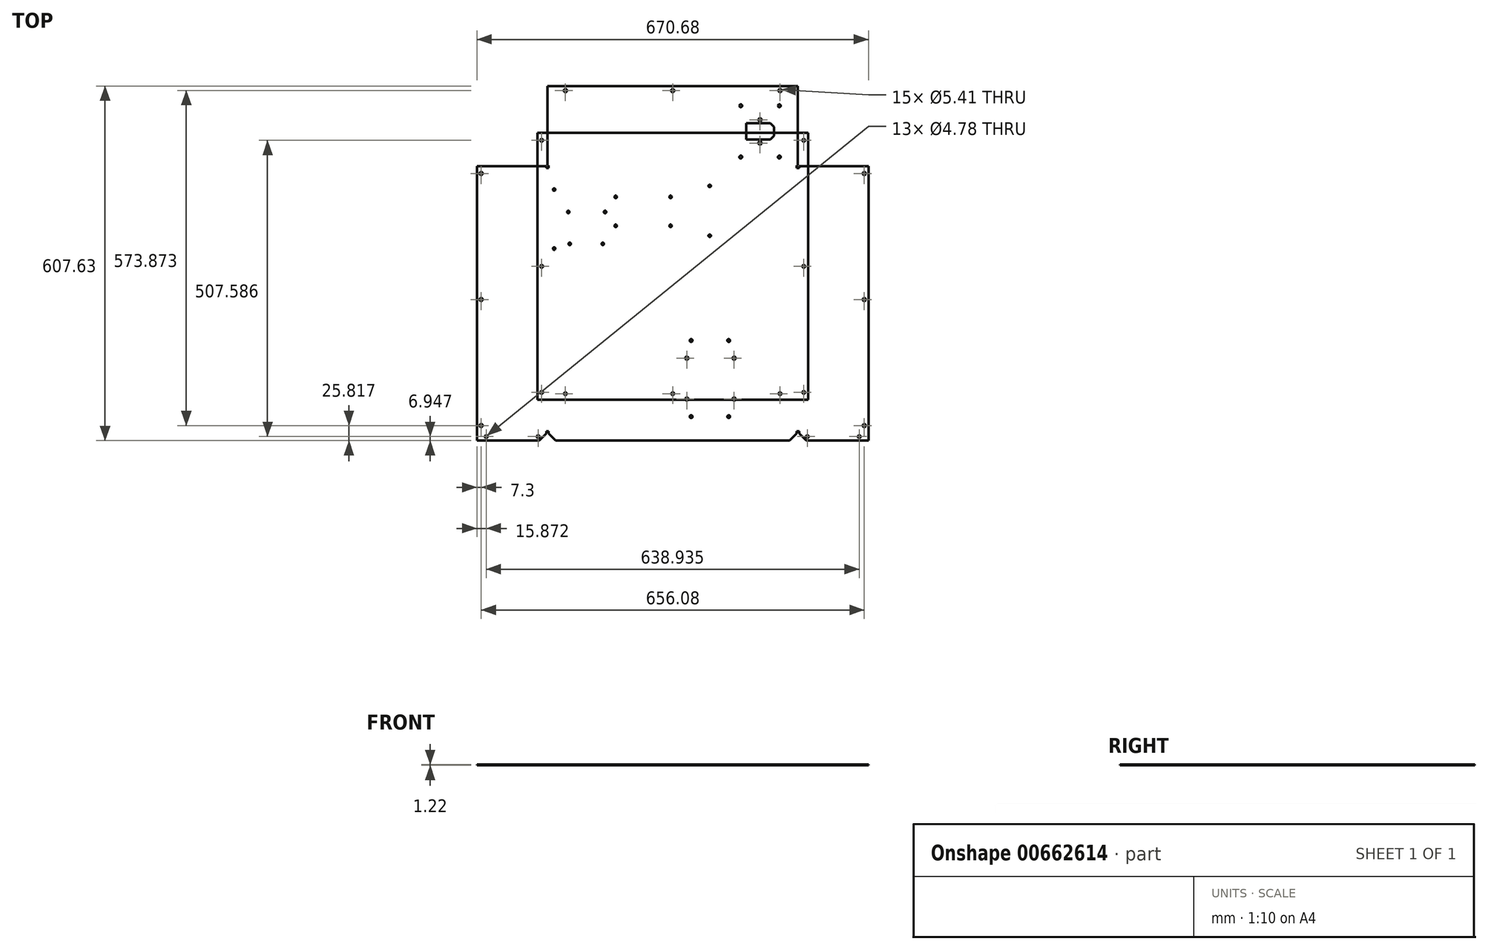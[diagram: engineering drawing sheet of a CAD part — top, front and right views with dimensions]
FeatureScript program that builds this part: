
annotation { "Feature Type Name" : "Feature", "Feature Type Description" : "" }
export const myFeature = defineFeature(function(context is Context, id is Id, definition is map)
    precondition{}
    {
        {
            var Q0;
            Q0=qCreatedBy(makeId("Top.planeOp"),FACE);
            var sketch = newSketch(context, id + "F0", { "sketchPlane" : qUnion([Q0])});
            skLineSegment(sketch, "E0", {"start": v(214.48, -268.44) * mm, "end": v(214.48, 182.35) * mm});
            skLineSegment(sketch, "E1", {"start": v(212.34, 184.5) * mm, "end": v(-212.34, 184.5) * mm});
            skLineSegment(sketch, "E2", {"start": v(335.34, 185.56) * mm, "end": v(216.63, 185.56) * mm});
            skLineSegment(sketch, "E3", {"start": v(335.34, 185.56) * mm, "end": v(335.34, -269.15) * mm});
            skLineSegment(sketch, "E4", {"start": v(335.34, -269.15) * mm, "end": v(216.65, -269.15) * mm});
            skLineSegment(sketch, "E5", {"start": v(216.65, -269.15) * mm, "end": v(216.65, -268.44) * mm});
            skLineSegment(sketch, "E6", {"start": v(216.65, -268.44) * mm, "end": v(215.91, -268.44) * mm});
            skLineSegment(sketch, "E7", {"start": v(215.91, 182.35) * mm, "end": v(215.91, -268.44) * mm});
            skLineSegment(sketch, "E8", {"start": v(215.91, 182.35) * mm, "end": v(216.63, 182.35) * mm});
            skLineSegment(sketch, "E9", {"start": v(216.63, 182.35) * mm, "end": v(216.63, 185.56) * mm});
            skCircle(sketch, "E10", {"center": v(328.04, 172.86) * mm, "radius": 2.7 * mm});
            skCircle(sketch, "E11", {"center": v(328.04, -43.04) * mm, "radius": 2.7 * mm});
            skCircle(sketch, "E12", {"center": v(328.04, -258.94) * mm, "radius": 2.7 * mm});
            skLineSegment(sketch, "E13", {"start": v(-335.34, -269.15) * mm, "end": v(-216.65, -269.15) * mm});
            skLineSegment(sketch, "E14", {"start": v(-335.34, -269.15) * mm, "end": v(-335.34, 185.56) * mm});
            skLineSegment(sketch, "E15", {"start": v(-335.34, 185.56) * mm, "end": v(-216.63, 185.56) * mm});
            skLineSegment(sketch, "E16", {"start": v(-216.63, 185.56) * mm, "end": v(-216.63, 182.35) * mm});
            skLineSegment(sketch, "E17", {"start": v(-215.91, -268.44) * mm, "end": v(-215.91, 182.35) * mm});
            skLineSegment(sketch, "E18", {"start": v(-215.91, -268.44) * mm, "end": v(-216.65, -268.44) * mm});
            skLineSegment(sketch, "E19", {"start": v(-216.65, -268.44) * mm, "end": v(-216.65, -269.15) * mm});
            skCircle(sketch, "E20", {"center": v(-328.04, 172.86) * mm, "radius": 2.7 * mm});
            skCircle(sketch, "E21", {"center": v(-328.04, -43.04) * mm, "radius": 2.7 * mm});
            skCircle(sketch, "E22", {"center": v(-328.04, -258.94) * mm, "radius": 2.7 * mm});
            skLineSegment(sketch, "E23", {"start": v(-216.63, 182.35) * mm, "end": v(-215.91, 182.35) * mm});
            skLineSegment(sketch, "E24", {"start": v(-228.68, -284.76) * mm, "end": v(-216.64, -272.72) * mm});
            skLineSegment(sketch, "E25", {"start": v(-335.34, -284.76) * mm, "end": v(-228.68, -284.76) * mm});
            skLineSegment(sketch, "E26", {"start": v(-335.34, -272.01) * mm, "end": v(-335.34, -284.76) * mm});
            skLineSegment(sketch, "E27", {"start": v(-335.34, -272.01) * mm, "end": v(-216.65, -272.01) * mm});
            skLineSegment(sketch, "E28", {"start": v(-216.65, -272.01) * mm, "end": v(-216.65, -272.72) * mm});
            skLineSegment(sketch, "E29", {"start": v(-216.65, -272.72) * mm, "end": v(-216.64, -272.72) * mm});
            skCircle(sketch, "E30", {"center": v(-230.57, -277.81) * mm, "radius": 2.39 * mm});
            skCircle(sketch, "E31", {"center": v(-319.47, -277.81) * mm, "radius": 2.39 * mm});
            skLineSegment(sketch, "E32", {"start": v(216.65, -272.01) * mm, "end": v(216.65, -269.15) * mm});
            skLineSegment(sketch, "E33", {"start": v(335.34, -269.15) * mm, "end": v(335.34, -272.01) * mm});
            skLineSegment(sketch, "E34", {"start": v(335.34, -272.01) * mm, "end": v(216.65, -272.01) * mm});
            skLineSegment(sketch, "E35", {"start": v(-216.65, -269.15) * mm, "end": v(-216.65, -272.01) * mm});
            skLineSegment(sketch, "E36", {"start": v(-335.34, -272.01) * mm, "end": v(-335.34, -269.15) * mm});
            skLineSegment(sketch, "E37", {"start": v(-214.3, 304.14) * mm, "end": v(214.3, 304.14) * mm});
            skLineSegment(sketch, "E38", {"start": v(214.3, 304.14) * mm, "end": v(214.3, 186.64) * mm});
            skLineSegment(sketch, "E39", {"start": v(214.3, 186.64) * mm, "end": v(212.34, 186.64) * mm});
            skLineSegment(sketch, "E40", {"start": v(212.34, 186.64) * mm, "end": v(212.34, 185.92) * mm});
            skLineSegment(sketch, "E41", {"start": v(-212.34, 185.92) * mm, "end": v(212.34, 185.92) * mm});
            skLineSegment(sketch, "E42", {"start": v(-212.34, 185.92) * mm, "end": v(-212.34, 186.64) * mm});
            skLineSegment(sketch, "E43", {"start": v(-212.34, 186.64) * mm, "end": v(-214.3, 186.64) * mm});
            skLineSegment(sketch, "E44", {"start": v(125.77, 231.19) * mm, "end": v(166.92, 231.19) * mm});
            skLineSegment(sketch, "E45", {"start": v(166.92, 231.19) * mm, "end": v(173.27, 237.54) * mm});
            skLineSegment(sketch, "E46", {"start": v(173.27, 237.54) * mm, "end": v(173.27, 252.52) * mm});
            skLineSegment(sketch, "E47", {"start": v(173.27, 252.52) * mm, "end": v(166.92, 258.87) * mm});
            skLineSegment(sketch, "E48", {"start": v(166.92, 258.87) * mm, "end": v(125.77, 258.87) * mm});
            skLineSegment(sketch, "E49", {"start": v(125.77, 258.87) * mm, "end": v(125.77, 231.19) * mm});
            skCircle(sketch, "E50", {"center": v(149.52, 264.97) * mm, "radius": 2.7 * mm});
            skCircle(sketch, "E51", {"center": v(149.52, 225.1) * mm, "radius": 2.7 * mm});
            skCircle(sketch, "E52", {"center": v(182.55, 288.93) * mm, "radius": 2.4 * mm});
            skCircle(sketch, "E53", {"center": v(182.55, 201.13) * mm, "radius": 2.4 * mm});
            skCircle(sketch, "E54", {"center": v(116.48, 288.93) * mm, "radius": 2.4 * mm});
            skCircle(sketch, "E55", {"center": v(116.48, 201.13) * mm, "radius": 2.4 * mm});
            skLineSegment(sketch, "E56", {"start": v(-214.3, 304.14) * mm, "end": v(-214.3, 186.64) * mm});
            skLineSegment(sketch, "E57", {"start": v(-213.06, -268.44) * mm, "end": v(-215.91, -268.44) * mm});
            skLineSegment(sketch, "E58", {"start": v(-213.06, -268.44) * mm, "end": v(-213.06, 182.35) * mm});
            skLineSegment(sketch, "E59", {"start": v(-215.91, 182.35) * mm, "end": v(-213.06, 182.35) * mm});
            skLineSegment(sketch, "E60", {"start": v(-214.3, 307) * mm, "end": v(214.3, 307) * mm});
            skLineSegment(sketch, "E61", {"start": v(214.3, 307) * mm, "end": v(214.3, 304.14) * mm});
            skLineSegment(sketch, "E62", {"start": v(-214.3, 304.14) * mm, "end": v(-214.3, 307) * mm});
            skCircle(sketch, "E63", {"center": v(-183.8, 314.93) * mm, "radius": 2.7 * mm});
            skCircle(sketch, "E64", {"center": v(0, 314.93) * mm, "radius": 2.7 * mm});
            skLineSegment(sketch, "E65", {"start": v(214.3, 322.87) * mm, "end": v(-214.3, 322.87) * mm});
            skLineSegment(sketch, "E66", {"start": v(214.3, 307) * mm, "end": v(214.3, 322.87) * mm});
            skLineSegment(sketch, "E67", {"start": v(-214.3, 322.87) * mm, "end": v(-214.3, 307) * mm});
            skCircle(sketch, "E68", {"center": v(183.8, 314.93) * mm, "radius": 2.7 * mm});
            skLineSegment(sketch, "E69", {"start": v(-212.34, 183.07) * mm, "end": v(-212.34, 185.92) * mm});
            skLineSegment(sketch, "E70", {"start": v(212.34, 185.92) * mm, "end": v(212.34, 183.07) * mm});
            skLineSegment(sketch, "E71", {"start": v(-212.34, 183.07) * mm, "end": v(212.34, 183.07) * mm});
            skLineSegment(sketch, "E72", {"start": v(212.31, -269.15) * mm, "end": v(212.31, -272.01) * mm});
            skLineSegment(sketch, "E73", {"start": v(212.31, -272.01) * mm, "end": v(-212.31, -272.01) * mm});
            skLineSegment(sketch, "E74", {"start": v(-212.31, -272.01) * mm, "end": v(-212.31, -269.15) * mm});
            skLineSegment(sketch, "E75", {"start": v(212.31, -269.15) * mm, "end": v(-212.31, -269.15) * mm});
            skLineSegment(sketch, "E76", {"start": v(212.34, 182.35) * mm, "end": v(212.34, 183.07) * mm});
            skLineSegment(sketch, "E77", {"start": v(213.06, 182.35) * mm, "end": v(212.34, 182.35) * mm});
            skLineSegment(sketch, "E78", {"start": v(213.06, 182.35) * mm, "end": v(213.06, -268.44) * mm});
            skLineSegment(sketch, "E79", {"start": v(212.31, -268.44) * mm, "end": v(213.06, -268.44) * mm});
            skLineSegment(sketch, "E80", {"start": v(-212.31, -268.44) * mm, "end": v(-212.31, -269.15) * mm});
            skLineSegment(sketch, "E81", {"start": v(-212.34, 182.35) * mm, "end": v(-213.06, 182.35) * mm});
            skLineSegment(sketch, "E82", {"start": v(-212.34, 183.07) * mm, "end": v(-212.34, 182.35) * mm});
            skCircle(sketch, "E83", {"center": v(-203.02, 145.28) * mm, "radius": 2.1 * mm});
            skCircle(sketch, "E84", {"center": v(-203.02, 44.24) * mm, "radius": 2.1 * mm});
            skCircle(sketch, "E85", {"center": v(-176.36, 52.4) * mm, "radius": 2.1 * mm});
            skCircle(sketch, "E86", {"center": v(-119.8, 52.4) * mm, "radius": 2.1 * mm});
            skCircle(sketch, "E87", {"center": v(-97.68, 83.35) * mm, "radius": 2.1 * mm});
            skCircle(sketch, "E88", {"center": v(-178.86, 107) * mm, "radius": 2.1 * mm});
            skCircle(sketch, "E89", {"center": v(-115.92, 107) * mm, "radius": 2.1 * mm});
            skCircle(sketch, "E90", {"center": v(-97.68, 132.88) * mm, "radius": 2.1 * mm});
            skCircle(sketch, "E91", {"center": v(-3.7, 132.88) * mm, "radius": 2.1 * mm});
            skCircle(sketch, "E92", {"center": v(63.33, 66.23) * mm, "radius": 2.1 * mm});
            skCircle(sketch, "E93", {"center": v(63.32, 151.64) * mm, "radius": 2.1 * mm});
            skCircle(sketch, "E94", {"center": v(-3.7, 83.35) * mm, "radius": 2.1 * mm});
            skCircle(sketch, "E95", {"center": v(24.15, -143.4) * mm, "radius": 2.7 * mm});
            skCircle(sketch, "E96", {"center": v(24.15, -213.4) * mm, "radius": 2.7 * mm});
            skCircle(sketch, "E97", {"center": v(105.15, -213.4) * mm, "radius": 2.7 * mm});
            skCircle(sketch, "E98", {"center": v(105.15, -143.4) * mm, "radius": 2.7 * mm});
            skCircle(sketch, "E99", {"center": v(31.5, -243.62) * mm, "radius": 2.4 * mm});
            skCircle(sketch, "E100", {"center": v(95.85, -243.62) * mm, "radius": 2.4 * mm});
            skCircle(sketch, "E101", {"center": v(31.5, -113.2) * mm, "radius": 2.4 * mm});
            skCircle(sketch, "E102", {"center": v(95.85, -113.2) * mm, "radius": 2.4 * mm});
            skLineSegment(sketch, "E103", {"start": v(212.31, -269.15) * mm, "end": v(212.31, -268.44) * mm});
            skLineSegment(sketch, "E104", {"start": v(-213.06, -268.44) * mm, "end": v(-212.31, -268.44) * mm});
            skLineSegment(sketch, "E105", {"start": v(215.91, -268.44) * mm, "end": v(213.06, -268.44) * mm});
            skLineSegment(sketch, "E106", {"start": v(213.06, 182.35) * mm, "end": v(215.91, 182.35) * mm});
            skLineSegment(sketch, "E107", {"start": v(335.34, -284.76) * mm, "end": v(335.34, -272.01) * mm});
            skLineSegment(sketch, "E108", {"start": v(228.68, -284.76) * mm, "end": v(335.34, -284.76) * mm});
            skLineSegment(sketch, "E109", {"start": v(216.65, -272.72) * mm, "end": v(216.65, -272.01) * mm});
            skCircle(sketch, "E110", {"center": v(230.57, -277.81) * mm, "radius": 2.39 * mm});
            skCircle(sketch, "E111", {"center": v(319.47, -277.81) * mm, "radius": 2.39 * mm});
            skLineSegment(sketch, "E112", {"start": v(216.64, -272.72) * mm, "end": v(228.68, -284.76) * mm});
            skLineSegment(sketch, "E113", {"start": v(216.64, -272.72) * mm, "end": v(216.65, -272.72) * mm});
            skLineSegment(sketch, "E114", {"start": v(212.31, -272.01) * mm, "end": v(212.31, -272.72) * mm});
            skLineSegment(sketch, "E115", {"start": v(-212.31, -272.72) * mm, "end": v(-212.31, -272.01) * mm});
            skLineSegment(sketch, "E116", {"start": v(-200.29, -284.76) * mm, "end": v(200.29, -284.76) * mm});
            skLineSegment(sketch, "E117", {"start": v(-200.29, -284.76) * mm, "end": v(-212.32, -272.72) * mm});
            skLineSegment(sketch, "E118", {"start": v(-212.32, -272.72) * mm, "end": v(-212.31, -272.72) * mm});
            skLineSegment(sketch, "E119", {"start": v(212.31, -272.72) * mm, "end": v(212.32, -272.72) * mm});
            skLineSegment(sketch, "E120", {"start": v(212.32, -272.72) * mm, "end": v(200.29, -284.76) * mm});
            skLineSegment(sketch, "E121", {"start": v(212.31, -270.58) * mm, "end": v(-212.31, -270.58) * mm});
            skLineSegment(sketch, "E122", {"start": v(-214.48, -268.44) * mm, "end": v(-214.48, 182.35) * mm});
            skLineSegment(sketch, "E123", {"start": v(-214.3, 305.56) * mm, "end": v(214.3, 305.56) * mm});
            skLineSegment(sketch, "E124", {"start": v(335.34, -270.58) * mm, "end": v(216.65, -270.58) * mm});
            skLineSegment(sketch, "E125", {"start": v(-335.34, -270.58) * mm, "end": v(-216.65, -270.58) * mm});
            skSolve(sketch);
        }
        {
            var Q0;
            Q0=makeQuery(id+"F0.imprint","IMPRINT",FACE,{"disambiguationData":[TD([[makeQuery(id+"F0.imprint","IMPRINT",EDGE,{"derivedFrom":sQuery(id+"F0.wireOp",EDGE,"E13")}),1.0]])]});
            var Q1;
            {var subQ0=sQuery(id+"F0.wireOp",EDGE,"E13");Q1=makeQuery(id+"F0.imprint","IMPRINT",FACE,{"disambiguationData":[TD([[makeQuery(id+"F0.imprint","IMPRINT",EDGE,{"derivedFrom":subQ0}),-1.0]])]});}
            var Q2;
            {var subQ0=sQuery(id+"F0.wireOp",EDGE,"E27");Q2=makeQuery(id+"F0.imprint","IMPRINT",FACE,{"disambiguationData":[TD([[makeQuery(id+"F0.imprint","IMPRINT",EDGE,{"derivedFrom":subQ0}),1.0]])]});}
            var Q3;
            Q3=makeQuery(id+"F0.imprint","IMPRINT",FACE,{"disambiguationData":[TD([[makeQuery(id+"F0.imprint","IMPRINT",EDGE,{"derivedFrom":sQuery(id+"F0.wireOp",EDGE,"E24")}),1.0]])]});
            var Q4;
            {var subQ0=sQuery(id+"F0.wireOp",EDGE,"E17");Q4=makeQuery(id+"F0.imprint","IMPRINT",FACE,{"disambiguationData":[TD([[makeQuery(id+"F0.imprint","IMPRINT",EDGE,{"derivedFrom":subQ0}),-1.0]])]});}
            var Q5;
            {var subQ0=sQuery(id+"F0.wireOp",EDGE,"E58");Q5=makeQuery(id+"F0.imprint","IMPRINT",FACE,{"disambiguationData":[TD([[makeQuery(id+"F0.imprint","IMPRINT",EDGE,{"derivedFrom":subQ0}),1.0]])]});}
            var Q6;
            {var subQ0=sQuery(id+"F0.wireOp",EDGE,"E75");Q6=makeQuery(id+"F0.imprint","IMPRINT",FACE,{"disambiguationData":[TD([[makeQuery(id+"F0.imprint","IMPRINT",EDGE,{"derivedFrom":subQ0}),1.0]])]});}
            var Q7;
            {var subQ0=sQuery(id+"F0.wireOp",EDGE,"E73");Q7=makeQuery(id+"F0.imprint","IMPRINT",FACE,{"disambiguationData":[TD([[makeQuery(id+"F0.imprint","IMPRINT",EDGE,{"derivedFrom":subQ0}),-1.0]])]});}
            var Q8;
            Q8=makeQuery(id+"F0.imprint","IMPRINT",FACE,{"disambiguationData":[TD([[makeQuery(id+"F0.imprint","IMPRINT",EDGE,{"derivedFrom":sQuery(id+"F0.wireOp",EDGE,"E73")}),1.0]])]});
            var Q9;
            Q9=makeQuery(id+"F0.imprint","IMPRINT",FACE,{"disambiguationData":[TD([[makeQuery(id+"F0.imprint","IMPRINT",EDGE,{"derivedFrom":sQuery(id+"F0.wireOp",EDGE,"E58")}),-1.0]])]});
            var Q10;
            {var subQ0=sQuery(id+"F0.wireOp",EDGE,"E0");Q10=makeQuery(id+"F0.imprint","IMPRINT",FACE,{"disambiguationData":[TD([[makeQuery(id+"F0.imprint","IMPRINT",EDGE,{"derivedFrom":subQ0}),1.0]])]});}
            var Q11;
            {var subQ0=sQuery(id+"F0.wireOp",EDGE,"E0");Q11=makeQuery(id+"F0.imprint","IMPRINT",FACE,{"disambiguationData":[TD([[makeQuery(id+"F0.imprint","IMPRINT",EDGE,{"derivedFrom":subQ0}),-1.0]])]});}
            var Q12;
            Q12=makeQuery(id+"F0.imprint","IMPRINT",FACE,{"disambiguationData":[TD([[makeQuery(id+"F0.imprint","IMPRINT",EDGE,{"derivedFrom":sQuery(id+"F0.wireOp",EDGE,"E2")}),1.0]])]});
            var Q13;
            {var subQ0=sQuery(id+"F0.wireOp",EDGE,"E4");Q13=makeQuery(id+"F0.imprint","IMPRINT",FACE,{"disambiguationData":[TD([[makeQuery(id+"F0.imprint","IMPRINT",EDGE,{"derivedFrom":subQ0}),1.0]])]});}
            var Q14;
            {var subQ0=sQuery(id+"F0.wireOp",EDGE,"E34");Q14=makeQuery(id+"F0.imprint","IMPRINT",FACE,{"disambiguationData":[TD([[makeQuery(id+"F0.imprint","IMPRINT",EDGE,{"derivedFrom":subQ0}),-1.0]])]});}
            var Q15;
            Q15=makeQuery(id+"F0.imprint","IMPRINT",FACE,{"disambiguationData":[TD([[makeQuery(id+"F0.imprint","IMPRINT",EDGE,{"derivedFrom":sQuery(id+"F0.wireOp",EDGE,"E34")}),1.0]])]});
            var Q16;
            Q16=makeQuery(id+"F0.imprint","IMPRINT",FACE,{"disambiguationData":[TD([[makeQuery(id+"F0.imprint","IMPRINT",EDGE,{"derivedFrom":sQuery(id+"F0.wireOp",EDGE,"E37")}),-1.0]])]});
            var Q17;
            {var subQ0=sQuery(id+"F0.wireOp",EDGE,"E1");Q17=makeQuery(id+"F0.imprint","IMPRINT",FACE,{"disambiguationData":[TD([[makeQuery(id+"F0.imprint","IMPRINT",EDGE,{"derivedFrom":subQ0}),-1.0]])]});}
            var Q18;
            {var subQ0=sQuery(id+"F0.wireOp",EDGE,"E1");Q18=makeQuery(id+"F0.imprint","IMPRINT",FACE,{"disambiguationData":[TD([[makeQuery(id+"F0.imprint","IMPRINT",EDGE,{"derivedFrom":subQ0}),1.0]])]});}
            var Q19;
            Q19=makeQuery(id+"F0.imprint","IMPRINT",FACE,{"disambiguationData":[TD([[makeQuery(id+"F0.imprint","IMPRINT",EDGE,{"derivedFrom":sQuery(id+"F0.wireOp",EDGE,"E60")}),1.0]])]});
            var Q20;
            {var subQ0=sQuery(id+"F0.wireOp",EDGE,"E60");Q20=makeQuery(id+"F0.imprint","IMPRINT",FACE,{"disambiguationData":[TD([[makeQuery(id+"F0.imprint","IMPRINT",EDGE,{"derivedFrom":subQ0}),-1.0]])]});}
            var Q21;
            {var subQ0=sQuery(id+"F0.wireOp",EDGE,"E37");Q21=makeQuery(id+"F0.imprint","IMPRINT",FACE,{"disambiguationData":[TD([[makeQuery(id+"F0.imprint","IMPRINT",EDGE,{"derivedFrom":subQ0}),1.0]])]});}
            extrude(context, id + "F1", {"entities" : qUnion([Q0, Q1, Q2, Q3, Q4, Q5, Q6, Q7, Q8, Q9, Q10, Q11, Q12, Q13, Q14, Q15, Q16, Q17, Q18, Q19, Q20, Q21]), "depth" : 1.22 * mm, "offsetDistance" : 25.4 * mm});
        }
        {
            var Q0;
            Q0=qCreatedBy(makeId("Top.planeOp"),FACE);
            var sketch = newSketch(context, id + "F2", { "sketchPlane" : qUnion([Q0])});
            skLineSegment(sketch, "E126", {"start": v(-215.7, 242.47) * mm, "end": v(-215.7, -214.73) * mm});
            skLineSegment(sketch, "E127", {"start": v(215.7, 242.47) * mm, "end": v(215.7, -214.73) * mm});
            skLineSegment(sketch, "E128", {"start": v(-231.74, 242.47) * mm, "end": v(-231.74, -214.73) * mm});
            skLineSegment(sketch, "E129", {"start": v(-217.13, 242.47) * mm, "end": v(-217.13, -214.73) * mm});
            skLineSegment(sketch, "E130", {"start": v(-231.74, -214.73) * mm, "end": v(-217.13, -214.73) * mm});
            skCircle(sketch, "E131", {"center": v(-224.43, 13.87) * mm, "radius": 2.39 * mm});
            skCircle(sketch, "E132", {"center": v(-224.43, 229.77) * mm, "radius": 2.39 * mm});
            skCircle(sketch, "E133", {"center": v(-224.43, -202.03) * mm, "radius": 2.39 * mm});
            skLineSegment(sketch, "E134", {"start": v(-217.13, 242.47) * mm, "end": v(-231.74, 242.47) * mm});
            skLineSegment(sketch, "E135", {"start": v(-214.27, 242.47) * mm, "end": v(-214.27, -214.73) * mm});
            skLineSegment(sketch, "E136", {"start": v(-214.27, -214.73) * mm, "end": v(-217.13, -214.73) * mm});
            skLineSegment(sketch, "E137", {"start": v(-217.13, 242.47) * mm, "end": v(-214.27, 242.47) * mm});
            skLineSegment(sketch, "E138", {"start": v(214.27, -214.73) * mm, "end": v(214.27, 242.47) * mm});
            skLineSegment(sketch, "E139", {"start": v(-214.27, -214.73) * mm, "end": v(214.27, -214.73) * mm});
            skCircle(sketch, "E140", {"center": v(0, -204.3) * mm, "radius": 2.39 * mm});
            skCircle(sketch, "E141", {"center": v(183.8, -204.3) * mm, "radius": 2.39 * mm});
            skCircle(sketch, "E142", {"center": v(-183.8, -204.3) * mm, "radius": 2.39 * mm});
            skLineSegment(sketch, "E143", {"start": v(214.27, 242.47) * mm, "end": v(-214.27, 242.47) * mm});
            skLineSegment(sketch, "E144", {"start": v(217.13, -214.73) * mm, "end": v(217.13, 242.47) * mm});
            skLineSegment(sketch, "E145", {"start": v(231.74, -214.73) * mm, "end": v(231.74, 242.47) * mm});
            skCircle(sketch, "E146", {"center": v(224.43, 229.77) * mm, "radius": 2.39 * mm});
            skLineSegment(sketch, "E147", {"start": v(231.74, 242.47) * mm, "end": v(217.13, 242.47) * mm});
            skCircle(sketch, "E148", {"center": v(224.43, 13.87) * mm, "radius": 2.39 * mm});
            skLineSegment(sketch, "E149", {"start": v(217.13, -214.73) * mm, "end": v(231.74, -214.73) * mm});
            skCircle(sketch, "E150", {"center": v(224.43, -202.03) * mm, "radius": 2.39 * mm});
            skLineSegment(sketch, "E151", {"start": v(217.13, -214.73) * mm, "end": v(214.27, -214.73) * mm});
            skLineSegment(sketch, "E152", {"start": v(214.27, 242.47) * mm, "end": v(217.13, 242.47) * mm});
            skSolve(sketch);
        }
        {
            var Q0;
            Q0=makeQuery(id+"F2.imprint","IMPRINT",FACE,{"disambiguationData":[TD([[makeQuery(id+"F2.imprint","IMPRINT",EDGE,{"derivedFrom":sQuery(id+"F2.wireOp",EDGE,"E128")}),1.0]])]});
            var Q1;
            {var subQ0=sQuery(id+"F2.wireOp",EDGE,"E126");Q1=makeQuery(id+"F2.imprint","IMPRINT",FACE,{"disambiguationData":[TD([[makeQuery(id+"F2.imprint","IMPRINT",EDGE,{"derivedFrom":subQ0}),-1.0]])]});}
            var Q2;
            {var subQ0=sQuery(id+"F2.wireOp",EDGE,"E126");Q2=makeQuery(id+"F2.imprint","IMPRINT",FACE,{"disambiguationData":[TD([[makeQuery(id+"F2.imprint","IMPRINT",EDGE,{"derivedFrom":subQ0}),1.0]])]});}
            var Q3;
            Q3=makeQuery(id+"F2.imprint","IMPRINT",FACE,{"disambiguationData":[TD([[makeQuery(id+"F2.imprint","IMPRINT",EDGE,{"derivedFrom":sQuery(id+"F2.wireOp",EDGE,"E135")}),1.0]])]});
            var Q4;
            {var subQ0=sQuery(id+"F2.wireOp",EDGE,"E127");Q4=makeQuery(id+"F2.imprint","IMPRINT",FACE,{"disambiguationData":[TD([[makeQuery(id+"F2.imprint","IMPRINT",EDGE,{"derivedFrom":subQ0}),-1.0]])]});}
            var Q5;
            {var subQ0=sQuery(id+"F2.wireOp",EDGE,"E127");Q5=makeQuery(id+"F2.imprint","IMPRINT",FACE,{"disambiguationData":[TD([[makeQuery(id+"F2.imprint","IMPRINT",EDGE,{"derivedFrom":subQ0}),1.0]])]});}
            var Q6;
            Q6=makeQuery(id+"F2.imprint","IMPRINT",FACE,{"disambiguationData":[TD([[makeQuery(id+"F2.imprint","IMPRINT",EDGE,{"derivedFrom":sQuery(id+"F2.wireOp",EDGE,"E144")}),-1.0]])]});
            extrude(context, id + "F3", {"entities" : qUnion([Q0, Q1, Q2, Q3, Q4, Q5, Q6]), "depth" : 1.22 * mm, "offsetDistance" : 25.4 * mm});
        }
    });
